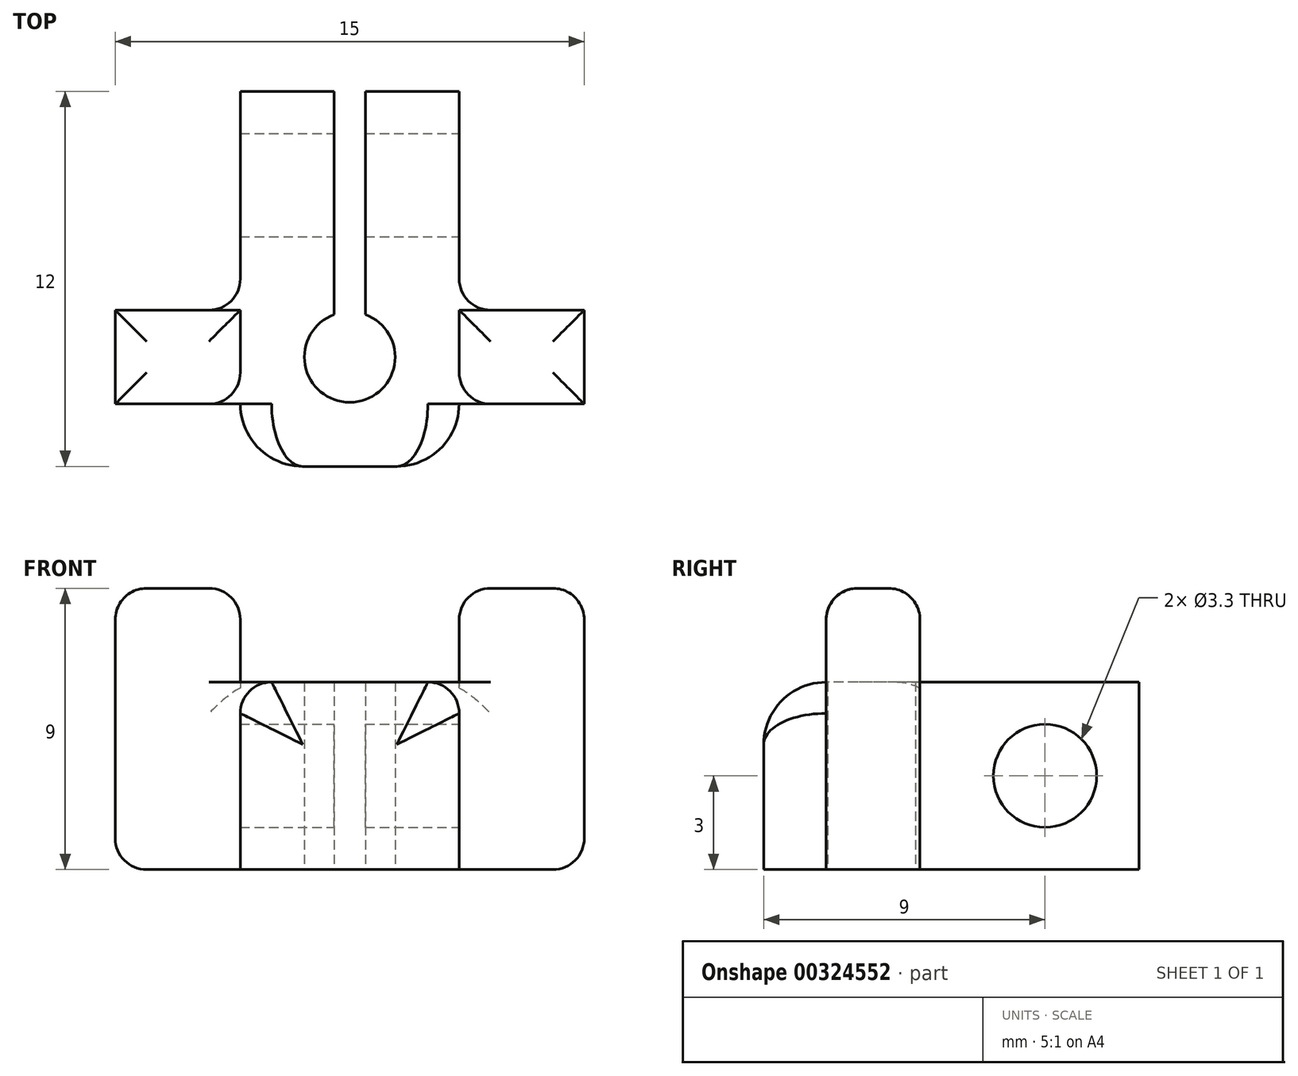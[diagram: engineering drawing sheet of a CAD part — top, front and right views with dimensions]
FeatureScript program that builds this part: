
annotation { "Feature Type Name" : "Feature", "Feature Type Description" : "" }
export const myFeature = defineFeature(function(context is Context, id is Id, definition is map)
    precondition{}
    {
        {
            var Q0;
            Q0=qCreatedBy(makeId("Top.planeOp"),FACE);
            var sketch = newSketch(context, id + "F0", { "sketchPlane" : qUnion([Q0])});
            skLineSegment(sketch, "E0.bottom", {"start": v(-3.5, 8.5) * mm, "end": v(3.5, 8.5) * mm});
            skLineSegment(sketch, "E0.top", {"start": v(-3.5, -3.5) * mm, "end": v(3.5, -3.5) * mm});
            skLineSegment(sketch, "E0.left", {"start": v(-3.5, 8.5) * mm, "end": v(-3.5, -3.5) * mm});
            skLineSegment(sketch, "E0.right", {"start": v(3.5, 8.5) * mm, "end": v(3.5, -3.5) * mm});
            skCircle(sketch, "E1", {"center": v(0, 0) * mm, "radius": 1.45 * mm});
            skLineSegment(sketch, "E2", {"start": v(0, 8.5) * mm, "end": v(0, -3.5) * mm, "construction": true});
            skLineSegment(sketch, "E3.bottom", {"start": v(-0.5, 8.5) * mm, "end": v(0.5, 8.5) * mm});
            skLineSegment(sketch, "E3.top", {"start": v(-0.5, 1.36) * mm, "end": v(0.5, 1.36) * mm});
            skLineSegment(sketch, "E3.left", {"start": v(-0.5, 8.5) * mm, "end": v(-0.5, 1.36) * mm});
            skLineSegment(sketch, "E3.right", {"start": v(0.5, 8.5) * mm, "end": v(0.5, 1.36) * mm});
            skSolve(sketch);
        }
        {
            var Q0;
            Q0=makeQuery(id+"F0.imprint","IMPRINT",FACE,{"disambiguationData":[TD([[makeQuery(id+"F0.imprint","IMPRINT",EDGE,{"derivedFrom":sQuery(id+"F0.wireOp",EDGE,"E0.top")}),1.0]])]});
            extrude(context, id + "F1", {"entities" : qUnion([Q0]), "depth" : 6 * mm});
        }
        {
            var Q0;
            Q0=makeQuery(id+"F1.opExtrude","SWEPT_FACE",FACE,{"disambiguationData":[OSD([sQuery(id+"F0.wireOp",EDGE,"E0.right")])]});
            var sketch = newSketch(context, id + "F2", { "sketchPlane" : qUnion([Q0])});
            skCircle(sketch, "E4", {"center": v(5.5, 3) * mm, "radius": 1.65 * mm});
            skSolve(sketch);
        }
        {
            var Q0;
            Q0=makeQuery(id+"F2.imprint","IMPRINT",FACE,{"disambiguationData":[TD([[makeQuery(id+"F2.imprint","IMPRINT",EDGE,{"derivedFrom":sQuery(id+"F2.wireOp",EDGE,"E4")}),1.0]])]});
            extrude(context, id + "F3", {"entities" : qUnion([Q0]), "operationType" : NewBodyOperationType.REMOVE, "oppositeDirection" : true, "depth" : 25 * mm});
        }
        {
            var Q0;
            Q0=makeQuery(id+"F1.opExtrude","CAP_FACE",FACE,{"disambiguationData":[OSD([sQuery(id+"F0.wireOp",EDGE,"E0.bottom"),sQuery(id+"F0.wireOp",EDGE,"E0.top"),sQuery(id+"F0.wireOp",EDGE,"E0.left"),sQuery(id+"F0.wireOp",EDGE,"E0.right"),sQuery(id+"F0.wireOp",EDGE,"E1"),sQuery(id+"F0.wireOp",EDGE,"E3.left"),sQuery(id+"F0.wireOp",EDGE,"E3.right")])],"isStart":true});
            var sketch = newSketch(context, id + "F4", { "sketchPlane" : qUnion([Q0])});
            skLineSegment(sketch, "E5.bottom", {"start": v(-7.5, 1.5) * mm, "end": v(7.5, 1.5) * mm});
            skLineSegment(sketch, "E5.top", {"start": v(-7.5, -1.5) * mm, "end": v(7.5, -1.5) * mm});
            skLineSegment(sketch, "E5.left", {"start": v(-7.5, 1.5) * mm, "end": v(-7.5, -1.5) * mm});
            skLineSegment(sketch, "E5.right", {"start": v(7.5, 1.5) * mm, "end": v(7.5, -1.5) * mm});
            skLineSegment(sketch, "E6", {"start": v(0, 3.5) * mm, "end": v(0, 0) * mm, "construction": true});
            skLineSegment(sketch, "E7", {"start": v(-7.5, 0) * mm, "end": v(7.5, 0) * mm, "construction": true});
            skSolve(sketch);
        }
        {
            var Q0;
            {var subQ3=sQuery(id+"F4.wireOp",EDGE,"E5.right");Q0=makeQuery(id+"F4.imprint","IMPRINT",FACE,{"disambiguationData":[TD([[makeQuery(id+"F4.imprint","IMPRINT",EDGE,{"derivedFrom":subQ3}),-1.0]])]});}
            var Q1;
            {var subQ3=sQuery(id+"F4.wireOp",EDGE,"E5.left");Q1=makeQuery(id+"F4.imprint","IMPRINT",FACE,{"disambiguationData":[TD([[makeQuery(id+"F4.imprint","IMPRINT",EDGE,{"derivedFrom":subQ3}),1.0]])]});}
            extrude(context, id + "F5", {"entities" : qUnion([Q0, Q1]), "operationType" : NewBodyOperationType.ADD, "oppositeDirection" : true, "depth" : 9 * mm});
        }
        {
            var Q0;
            {var subQ0=sQuery(id+"F0.wireOp",EDGE,"E0.right");var subQ1=sQuery(id+"F4.wireOp",EDGE,"E5.top");Q0=makeQuery(id+"F5.boolean.opBoolean","SPLIT",EDGE,{"disambiguationData":[topologyDisambiguationEdgeConnected([makeQuery(id+"F1.opExtrude","SWEPT_FACE",FACE,{"disambiguationData":[OSD([subQ0])]})])],"derivedFrom":makeQuery(id+"F5.opExtrude","SWEPT_EDGE",EDGE,{"disambiguationData":[OSD([subQ0,subQ1])]})});}
            var Q1;
            {var subQ0=sQuery(id+"F0.wireOp",EDGE,"E0.right");var subQ1=sQuery(id+"F4.wireOp",EDGE,"E5.bottom");Q1=makeQuery(id+"F5.boolean.opBoolean","SPLIT",EDGE,{"disambiguationData":[topologyDisambiguationEdgeConnected([makeQuery(id+"F1.opExtrude","SWEPT_FACE",FACE,{"disambiguationData":[OSD([subQ0])]})])],"derivedFrom":makeQuery(id+"F5.opExtrude","SWEPT_EDGE",EDGE,{"disambiguationData":[OSD([subQ0,subQ1])]})});}
            var Q2;
            {var subQ0=sQuery(id+"F0.wireOp",EDGE,"E0.left");var subQ1=sQuery(id+"F4.wireOp",EDGE,"E5.bottom");Q2=makeQuery(id+"F5.boolean.opBoolean","SPLIT",EDGE,{"disambiguationData":[topologyDisambiguationEdgeConnected([makeQuery(id+"F1.opExtrude","SWEPT_FACE",FACE,{"disambiguationData":[OSD([subQ0])]})])],"derivedFrom":makeQuery(id+"F5.opExtrude","SWEPT_EDGE",EDGE,{"disambiguationData":[OSD([subQ0,subQ1])]})});}
            var Q3;
            {var subQ0=sQuery(id+"F0.wireOp",EDGE,"E0.left");var subQ1=sQuery(id+"F4.wireOp",EDGE,"E5.top");Q3=makeQuery(id+"F5.boolean.opBoolean","SPLIT",EDGE,{"disambiguationData":[topologyDisambiguationEdgeConnected([makeQuery(id+"F1.opExtrude","SWEPT_FACE",FACE,{"disambiguationData":[OSD([subQ0])]})])],"derivedFrom":makeQuery(id+"F5.opExtrude","SWEPT_EDGE",EDGE,{"disambiguationData":[OSD([subQ0,subQ1])]})});}
            fillet(context, id + "F6", {"entities" : qUnion([Q0, Q1, Q2, Q3]), "radius" : 1 * mm, "tangentPropagation" : true, "allowEdgeOverflow" : false});
        }
        {
            var Q0;
            Q0=makeQuery(id+"F5.opExtrude","CAP_EDGE",EDGE,{"disambiguationData":[OSD([sQuery(id+"F0.wireOp",EDGE,"E0.left")])],"isStart":false});
            var Q1;
            Q1=makeQuery(id+"F5.opExtrude","CAP_EDGE",EDGE,{"disambiguationData":[OSD([sQuery(id+"F0.wireOp",EDGE,"E0.right")])],"isStart":false});
            var Q2;
            Q2=makeQuery(id+"F5.opExtrude","CAP_EDGE",EDGE,{"disambiguationData":[OSD([sQuery(id+"F4.wireOp",EDGE,"E5.right")])],"isStart":false});
            var Q3;
            {var subQ0=sQuery(id+"F4.wireOp",EDGE,"E5.top");Q3=makeQuery(id+"F5.opExtrude","CAP_EDGE",EDGE,{"disambiguationData":[OSD([subQ0]),TDD([makeQuery(id+"F4.imprint","IMPRINT",EDGE,{"disambiguationData":[TD([[makeQuery(id+"F4.imprint","INTERSECT",VERTEX,{"derivedFrom":[subQ0,sQuery(id+"F4.wireOp",EDGE,"E5.right")]}),1.0]])],"derivedFrom":subQ0})])],"isStart":false});}
            var Q4;
            {var subQ0=sQuery(id+"F4.wireOp",EDGE,"E5.bottom");Q4=makeQuery(id+"F5.opExtrude","CAP_EDGE",EDGE,{"disambiguationData":[OSD([subQ0]),TDD([makeQuery(id+"F4.imprint","IMPRINT",EDGE,{"disambiguationData":[TD([[makeQuery(id+"F4.imprint","INTERSECT",VERTEX,{"derivedFrom":[subQ0,sQuery(id+"F4.wireOp",EDGE,"E5.right")]}),1.0]])],"derivedFrom":subQ0})])],"isStart":false});}
            var Q5;
            {var subQ0=sQuery(id+"F4.wireOp",EDGE,"E5.top");Q5=makeQuery(id+"F5.opExtrude","CAP_EDGE",EDGE,{"disambiguationData":[OSD([subQ0]),TDD([makeQuery(id+"F4.imprint","IMPRINT",EDGE,{"disambiguationData":[TD([[makeQuery(id+"F4.imprint","INTERSECT",VERTEX,{"derivedFrom":[subQ0,sQuery(id+"F4.wireOp",EDGE,"E5.left")]}),-1.0]])],"derivedFrom":subQ0})])],"isStart":false});}
            var Q6;
            Q6=makeQuery(id+"F5.opExtrude","CAP_EDGE",EDGE,{"disambiguationData":[OSD([sQuery(id+"F4.wireOp",EDGE,"E5.left")])],"isStart":false});
            var Q7;
            {var subQ0=sQuery(id+"F4.wireOp",EDGE,"E5.bottom");Q7=makeQuery(id+"F5.opExtrude","CAP_EDGE",EDGE,{"disambiguationData":[OSD([subQ0]),TDD([makeQuery(id+"F4.imprint","IMPRINT",EDGE,{"disambiguationData":[TD([[makeQuery(id+"F4.imprint","INTERSECT",VERTEX,{"derivedFrom":[subQ0,sQuery(id+"F4.wireOp",EDGE,"E5.left")]}),-1.0]])],"derivedFrom":subQ0})])],"isStart":false});}
            var Q8;
            Q8=makeQuery(id+"F5.opExtrude","CAP_EDGE",EDGE,{"disambiguationData":[OSD([sQuery(id+"F4.wireOp",EDGE,"E5.left")])],"isStart":true});
            var Q9;
            Q9=makeQuery(id+"F5.opExtrude","CAP_EDGE",EDGE,{"disambiguationData":[OSD([sQuery(id+"F4.wireOp",EDGE,"E5.right")])],"isStart":true});
            fillet(context, id + "F7", {"entities" : qUnion([Q0, Q1, Q2, Q3, Q4, Q5, Q6, Q7, Q8, Q9]), "radius" : 1 * mm, "tangentPropagation" : true, "allowEdgeOverflow" : false});
        }
        {
            var Q0;
            {var subQ0=sQuery(id+"F0.wireOp",EDGE,"E0.right");Q0=makeQuery(id+"F5.boolean.opBoolean","SPLIT",EDGE,{"disambiguationData":[topologyDisambiguationEdgeConnected([makeQuery(id+"F1.opExtrude","CAP_FACE",FACE,{"disambiguationData":[OSD([sQuery(id+"F0.wireOp",EDGE,"E0.bottom"),sQuery(id+"F0.wireOp",EDGE,"E0.top"),sQuery(id+"F0.wireOp",EDGE,"E0.left"),subQ0,sQuery(id+"F0.wireOp",EDGE,"E1"),sQuery(id+"F0.wireOp",EDGE,"E3.left"),sQuery(id+"F0.wireOp",EDGE,"E3.right")])],"isStart":false}),makeQuery(id+"F5.opExtrude","SWEPT_FACE",FACE,{"disambiguationData":[OSD([subQ0])]})])],"derivedFrom":makeQuery(id+"F1.opExtrude","CAP_EDGE",EDGE,{"disambiguationData":[OSD([subQ0])],"isStart":false})});}
            var Q1;
            {var subQ0=sQuery(id+"F0.wireOp",EDGE,"E0.left");Q1=makeQuery(id+"F5.boolean.opBoolean","SPLIT",EDGE,{"disambiguationData":[topologyDisambiguationEdgeConnected([makeQuery(id+"F1.opExtrude","CAP_FACE",FACE,{"disambiguationData":[OSD([sQuery(id+"F0.wireOp",EDGE,"E0.bottom"),sQuery(id+"F0.wireOp",EDGE,"E0.top"),subQ0,sQuery(id+"F0.wireOp",EDGE,"E0.right"),sQuery(id+"F0.wireOp",EDGE,"E1"),sQuery(id+"F0.wireOp",EDGE,"E3.left"),sQuery(id+"F0.wireOp",EDGE,"E3.right")])],"isStart":false}),makeQuery(id+"F5.opExtrude","SWEPT_FACE",FACE,{"disambiguationData":[OSD([subQ0])]})])],"derivedFrom":makeQuery(id+"F1.opExtrude","CAP_EDGE",EDGE,{"disambiguationData":[OSD([subQ0])],"isStart":false})});}
            var Q2;
            {var subQ0=sQuery(id+"F0.wireOp",EDGE,"E0.right");var subQ1=sQuery(id+"F4.wireOp",EDGE,"E5.top");Q2=makeQuery(id+"F6.opFillet","TWEAK_EDGE",EDGE,{"derivedFrom":[makeQuery(id+"F5.boolean.opBoolean","TWEAK_VERTEX",VERTEX,{"derivedFrom":[makeQuery(id+"F1.opExtrude","CAP_FACE",FACE,{"disambiguationData":[OSD([sQuery(id+"F0.wireOp",EDGE,"E0.bottom"),sQuery(id+"F0.wireOp",EDGE,"E0.top"),sQuery(id+"F0.wireOp",EDGE,"E0.left"),subQ0,sQuery(id+"F0.wireOp",EDGE,"E1"),sQuery(id+"F0.wireOp",EDGE,"E3.left"),sQuery(id+"F0.wireOp",EDGE,"E3.right")])],"isStart":false}),makeQuery(id+"F1.opExtrude","SWEPT_FACE",FACE,{"disambiguationData":[OSD([subQ0])]}),makeQuery(id+"F5.opExtrude","SWEPT_FACE",FACE,{"disambiguationData":[OSD([subQ1]),TDD([makeQuery(id+"F4.imprint","IMPRINT",EDGE,{"disambiguationData":[TD([[makeQuery(id+"F4.imprint","INTERSECT",VERTEX,{"derivedFrom":[subQ1,sQuery(id+"F4.wireOp",EDGE,"E5.right")]}),1.0]])],"derivedFrom":subQ1})])]}),makeQuery(id+"F5.opExtrude","SWEPT_FACE",FACE,{"disambiguationData":[OSD([subQ0])]})]})]});}
            var Q3;
            {var subQ0=sQuery(id+"F0.wireOp",EDGE,"E0.left");var subQ1=sQuery(id+"F4.wireOp",EDGE,"E5.top");Q3=makeQuery(id+"F6.opFillet","TWEAK_EDGE",EDGE,{"derivedFrom":[makeQuery(id+"F5.boolean.opBoolean","TWEAK_VERTEX",VERTEX,{"derivedFrom":[makeQuery(id+"F1.opExtrude","CAP_FACE",FACE,{"disambiguationData":[OSD([sQuery(id+"F0.wireOp",EDGE,"E0.bottom"),sQuery(id+"F0.wireOp",EDGE,"E0.top"),subQ0,sQuery(id+"F0.wireOp",EDGE,"E0.right"),sQuery(id+"F0.wireOp",EDGE,"E1"),sQuery(id+"F0.wireOp",EDGE,"E3.left"),sQuery(id+"F0.wireOp",EDGE,"E3.right")])],"isStart":false}),makeQuery(id+"F1.opExtrude","SWEPT_FACE",FACE,{"disambiguationData":[OSD([subQ0])]}),makeQuery(id+"F5.opExtrude","SWEPT_FACE",FACE,{"disambiguationData":[OSD([subQ1]),TDD([makeQuery(id+"F4.imprint","IMPRINT",EDGE,{"disambiguationData":[TD([[makeQuery(id+"F4.imprint","INTERSECT",VERTEX,{"derivedFrom":[subQ1,sQuery(id+"F4.wireOp",EDGE,"E5.left")]}),-1.0]])],"derivedFrom":subQ1})])]}),makeQuery(id+"F5.opExtrude","SWEPT_FACE",FACE,{"disambiguationData":[OSD([subQ0])]})]})]});}
            var Q4;
            {var subQ0=sQuery(id+"F0.wireOp",EDGE,"E0.right");var subQ1=sQuery(id+"F4.wireOp",EDGE,"E5.bottom");Q4=makeQuery(id+"F6.opFillet","TWEAK_EDGE",EDGE,{"derivedFrom":[makeQuery(id+"F5.boolean.opBoolean","TWEAK_VERTEX",VERTEX,{"derivedFrom":[makeQuery(id+"F1.opExtrude","CAP_FACE",FACE,{"disambiguationData":[OSD([sQuery(id+"F0.wireOp",EDGE,"E0.bottom"),sQuery(id+"F0.wireOp",EDGE,"E0.top"),sQuery(id+"F0.wireOp",EDGE,"E0.left"),subQ0,sQuery(id+"F0.wireOp",EDGE,"E1"),sQuery(id+"F0.wireOp",EDGE,"E3.left"),sQuery(id+"F0.wireOp",EDGE,"E3.right")])],"isStart":false}),makeQuery(id+"F1.opExtrude","SWEPT_FACE",FACE,{"disambiguationData":[OSD([subQ0])]}),makeQuery(id+"F5.opExtrude","SWEPT_FACE",FACE,{"disambiguationData":[OSD([subQ1]),TDD([makeQuery(id+"F4.imprint","IMPRINT",EDGE,{"disambiguationData":[TD([[makeQuery(id+"F4.imprint","INTERSECT",VERTEX,{"derivedFrom":[subQ1,sQuery(id+"F4.wireOp",EDGE,"E5.right")]}),1.0]])],"derivedFrom":subQ1})])]}),makeQuery(id+"F5.opExtrude","SWEPT_FACE",FACE,{"disambiguationData":[OSD([subQ0])]})]})]});}
            var Q5;
            {var subQ0=sQuery(id+"F0.wireOp",EDGE,"E0.left");var subQ1=sQuery(id+"F4.wireOp",EDGE,"E5.bottom");Q5=makeQuery(id+"F6.opFillet","TWEAK_EDGE",EDGE,{"derivedFrom":[makeQuery(id+"F5.boolean.opBoolean","TWEAK_VERTEX",VERTEX,{"derivedFrom":[makeQuery(id+"F1.opExtrude","CAP_FACE",FACE,{"disambiguationData":[OSD([sQuery(id+"F0.wireOp",EDGE,"E0.bottom"),sQuery(id+"F0.wireOp",EDGE,"E0.top"),subQ0,sQuery(id+"F0.wireOp",EDGE,"E0.right"),sQuery(id+"F0.wireOp",EDGE,"E1"),sQuery(id+"F0.wireOp",EDGE,"E3.left"),sQuery(id+"F0.wireOp",EDGE,"E3.right")])],"isStart":false}),makeQuery(id+"F1.opExtrude","SWEPT_FACE",FACE,{"disambiguationData":[OSD([subQ0])]}),makeQuery(id+"F5.opExtrude","SWEPT_FACE",FACE,{"disambiguationData":[OSD([subQ1]),TDD([makeQuery(id+"F4.imprint","IMPRINT",EDGE,{"disambiguationData":[TD([[makeQuery(id+"F4.imprint","INTERSECT",VERTEX,{"derivedFrom":[subQ1,sQuery(id+"F4.wireOp",EDGE,"E5.left")]}),-1.0]])],"derivedFrom":subQ1})])]}),makeQuery(id+"F5.opExtrude","SWEPT_FACE",FACE,{"disambiguationData":[OSD([subQ0])]})]})]});}
            fillet(context, id + "F8", {"entities" : qUnion([Q0, Q1, Q2, Q3, Q4, Q5]), "radius" : 1 * mm, "tangentPropagation" : true, "allowEdgeOverflow" : false});
        }
        {
            var Q0;
            Q0=makeQuery(id+"F1.opExtrude","SWEPT_EDGE",EDGE,{"disambiguationData":[OSD([sQuery(id+"F0.wireOp",EDGE,"E0.top"),sQuery(id+"F0.wireOp",EDGE,"E0.right")])]});
            var Q1;
            Q1=makeQuery(id+"F1.opExtrude","SWEPT_EDGE",EDGE,{"disambiguationData":[OSD([sQuery(id+"F0.wireOp",EDGE,"E0.top"),sQuery(id+"F0.wireOp",EDGE,"E0.left")])]});
            fillet(context, id + "F9", {"entities" : qUnion([Q0, Q1]), "radius" : 2 * mm, "tangentPropagation" : true, "allowEdgeOverflow" : false});
        }
    });
